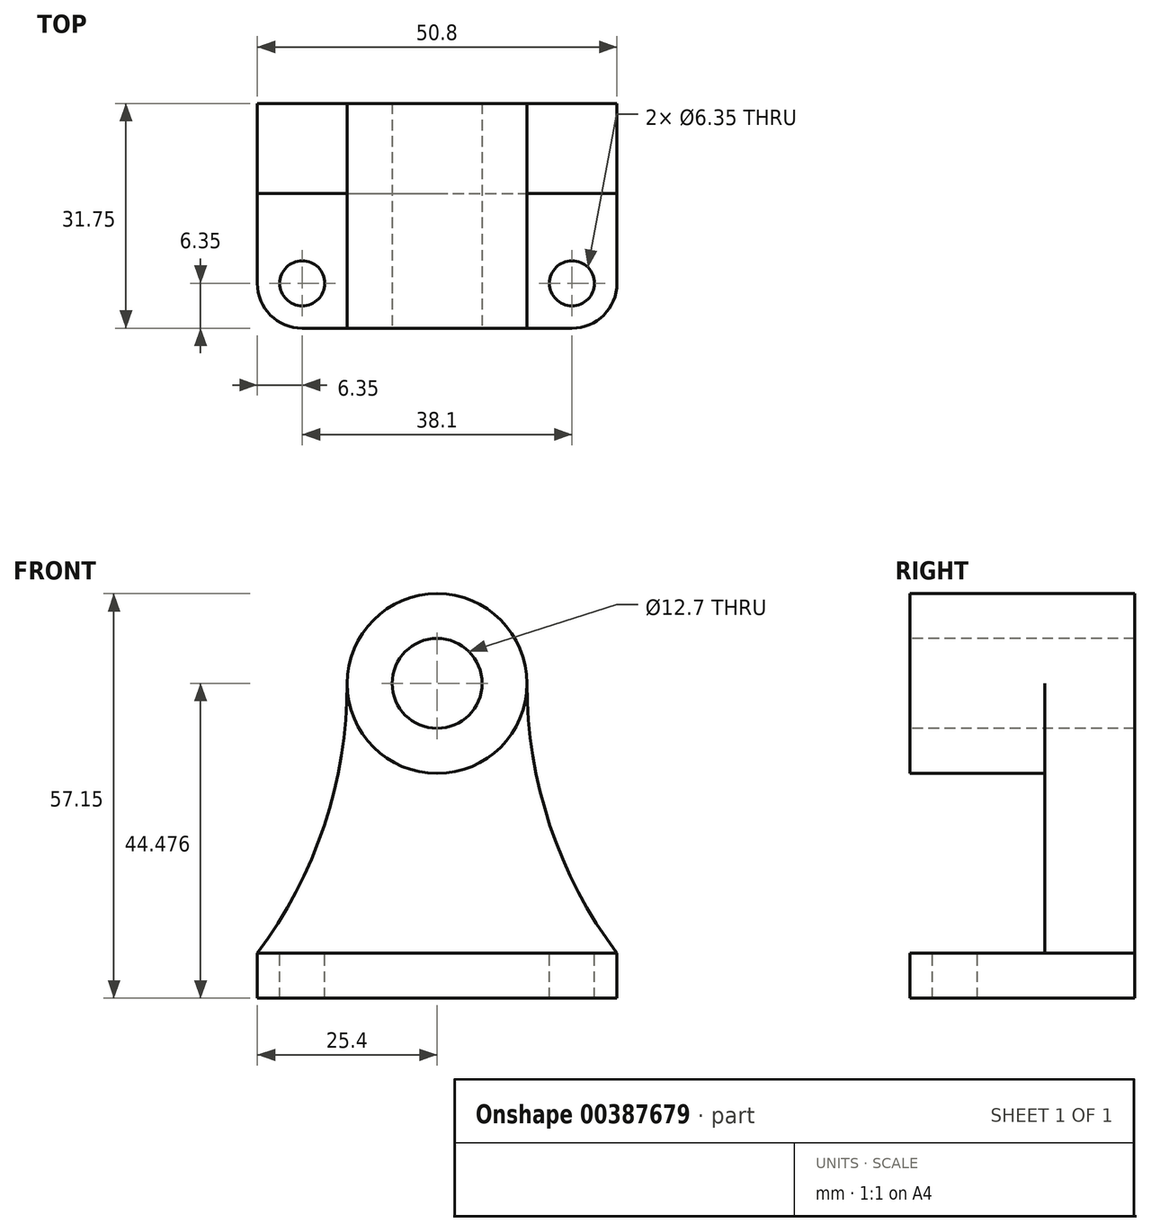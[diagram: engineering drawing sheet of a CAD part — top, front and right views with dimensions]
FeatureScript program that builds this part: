
annotation { "Feature Type Name" : "Feature", "Feature Type Description" : "" }
export const myFeature = defineFeature(function(context is Context, id is Id, definition is map)
    precondition{}
    {
        {
            var Q0;
            Q0=qCreatedBy(makeId("Front.planeOp"),FACE);
            var sketch = newSketch(context, id + "F0", { "sketchPlane" : qUnion([Q0])});
            skLineSegment(sketch, "E0", {"start": v(0, 0) * mm, "end": v(50.8, 0) * mm});
            skLineSegment(sketch, "E1", {"start": v(50.8, 0) * mm, "end": v(50.8, 6.35) * mm});
            skLineSegment(sketch, "E2", {"start": v(50.8, 6.35) * mm, "end": v(38.1, 6.35) * mm});
            skLineSegment(sketch, "E3", {"start": v(38.1, 6.35) * mm, "end": v(38.1, 57.15) * mm});
            skLineSegment(sketch, "E4", {"start": v(38.1, 57.15) * mm, "end": v(12.7, 57.15) * mm});
            skLineSegment(sketch, "E5", {"start": v(12.7, 57.15) * mm, "end": v(12.7, 6.35) * mm});
            skLineSegment(sketch, "E6", {"start": v(12.7, 6.35) * mm, "end": v(0, 6.35) * mm});
            skLineSegment(sketch, "E7", {"start": v(0, 6.35) * mm, "end": v(0, 0) * mm});
            skSolve(sketch);
        }
        {
            var Q0;
            Q0=makeQuery(id+"F0.imprint","IMPRINT",FACE,{"disambiguationData":[TD([[makeQuery(id+"F0.imprint","IMPRINT",EDGE,{"derivedFrom":sQuery(id+"F0.wireOp",EDGE,"E0")}),1.0]])]});
            extrude(context, id + "F1", {"entities" : qUnion([Q0]), "depth" : 31.75 * mm});
        }
        {
            var Q0;
            Q0=makeQuery(id+"F1.opExtrude","CAP_FACE",FACE,{"disambiguationData":[OSD([sQuery(id+"F0.wireOp",EDGE,"E0"),sQuery(id+"F0.wireOp",EDGE,"E1"),sQuery(id+"F0.wireOp",EDGE,"E2"),sQuery(id+"F0.wireOp",EDGE,"E3"),sQuery(id+"F0.wireOp",EDGE,"E4"),sQuery(id+"F0.wireOp",EDGE,"E5"),sQuery(id+"F0.wireOp",EDGE,"E6"),sQuery(id+"F0.wireOp",EDGE,"E7")])],"isStart":false});
            var sketch = newSketch(context, id + "F2", { "sketchPlane" : qUnion([Q0])});
            skCircle(sketch, "E8", {"center": v(25.4, 44.45) * mm, "radius": 12.7 * mm});
            skSolve(sketch);
        }
        {
            var Q0;
            {var subQ0=sQuery(id+"F2.wireOp",EDGE,"E8");var subQ1=makeQuery(id+"F1.opExtrude","CAP_EDGE",EDGE,{"disambiguationData":[OSD([sQuery(id+"F0.wireOp",EDGE,"E4")])],"isStart":false});var subQ2=makeQuery(id+"F2.imprint","INTERSECT",VERTEX,{"derivedFrom":[subQ1,subQ0]});Q0=makeQuery(id+"F2.imprint","IMPRINT",FACE,{"disambiguationData":[TD([[makeQuery(id+"F2.imprint","IMPRINT",EDGE,{"disambiguationData":[TD([[subQ2,-1.0]])],"derivedFrom":subQ0}),-1.0]])]});}
            var Q1;
            {var subQ0=sQuery(id+"F2.wireOp",EDGE,"E8");var subQ1=makeQuery(id+"F1.opExtrude","CAP_EDGE",EDGE,{"disambiguationData":[OSD([sQuery(id+"F0.wireOp",EDGE,"E4")])],"isStart":false});var subQ2=makeQuery(id+"F2.imprint","INTERSECT",VERTEX,{"derivedFrom":[subQ1,subQ0]});Q1=makeQuery(id+"F2.imprint","IMPRINT",FACE,{"disambiguationData":[TD([[makeQuery(id+"F2.imprint","IMPRINT",EDGE,{"disambiguationData":[TD([[subQ2,1.0]])],"derivedFrom":subQ0}),-1.0]])]});}
            extrude(context, id + "F3", {"entities" : qUnion([Q0, Q1]), "operationType" : NewBodyOperationType.REMOVE, "oppositeDirection" : true, "depth" : 31.75 * mm});
        }
        {
            var Q0;
            Q0=makeQuery(id+"F1.opExtrude","CAP_FACE",FACE,{"disambiguationData":[OSD([sQuery(id+"F0.wireOp",EDGE,"E0"),sQuery(id+"F0.wireOp",EDGE,"E1"),sQuery(id+"F0.wireOp",EDGE,"E2"),sQuery(id+"F0.wireOp",EDGE,"E3"),sQuery(id+"F0.wireOp",EDGE,"E4"),sQuery(id+"F0.wireOp",EDGE,"E5"),sQuery(id+"F0.wireOp",EDGE,"E6"),sQuery(id+"F0.wireOp",EDGE,"E7")])],"isStart":false});
            var sketch = newSketch(context, id + "F4", { "sketchPlane" : qUnion([Q0])});
            skCircle(sketch, "E9", {"center": v(25.4, 44.45) * mm, "radius": 12.7 * mm});
            skSolve(sketch);
        }
        {
            var Q0;
            Q0=makeQuery(id+"F4.imprint","IMPRINT",FACE,{"disambiguationData":[TD([[makeQuery(id+"F4.imprint","IMPRINT",EDGE,{"derivedFrom":makeQuery(id+"F1.opExtrude","CAP_EDGE",EDGE,{"disambiguationData":[OSD([sQuery(id+"F0.wireOp",EDGE,"E0")])],"isStart":false})}),1.0]])]});
            var sketch = newSketch(context, id + "F5", { "sketchPlane" : qUnion([Q0])});
            skLineSegment(sketch, "E10", {"start": v(12.7, 31.75) * mm, "end": v(38.1, 31.75) * mm});
            skSolve(sketch);
        }
        {
            var Q0;
            {var subQ0=sQuery(id+"F4.wireOp",EDGE,"E9");var subQ1=makeQuery(id+"F4.imprint","INTERSECT",VERTEX,{"derivedFrom":[makeQuery(id+"F1.opExtrude","CAP_EDGE",EDGE,{"disambiguationData":[OSD([sQuery(id+"F0.wireOp",EDGE,"E3")])],"isStart":false}),subQ0]});Q0=makeQuery(id+"F4.imprint","IMPRINT",FACE,{"disambiguationData":[TD([[makeQuery(id+"F4.imprint","IMPRINT",EDGE,{"disambiguationData":[TD([[subQ1,-1.0]])],"derivedFrom":subQ0}),1.0]])]});}
            var sketch = newSketch(context, id + "F6", { "sketchPlane" : qUnion([Q0])});
            skCircle(sketch, "E11", {"center": v(25.4, 44.48) * mm, "radius": 12.7 * mm});
            skSolve(sketch);
        }
        {
            var Q0;
            {var subQ0=sQuery(id+"F5.wireOp",EDGE,"E10");var subQ1=makeQuery(id+"F1.opExtrude","CAP_EDGE",EDGE,{"disambiguationData":[OSD([sQuery(id+"F0.wireOp",EDGE,"E3")])],"isStart":false});var subQ2=makeQuery(id+"F4.imprint","IMPRINT",EDGE,{"derivedFrom":subQ1});var subQ3=makeQuery(id+"F5.imprint","INTERSECT",VERTEX,{"derivedFrom":[subQ2,subQ0]});Q0=makeQuery(id+"F5.imprint","IMPRINT",FACE,{"disambiguationData":[TD([[makeQuery(id+"F5.imprint","IMPRINT",EDGE,{"disambiguationData":[TD([[subQ3,1.0]])],"derivedFrom":subQ0}),1.0]])]});}
            extrude(context, id + "F7", {"entities" : qUnion([Q0]), "operationType" : NewBodyOperationType.REMOVE, "oppositeDirection" : true, "depth" : 19.05 * mm});
        }
        {
            var Q0;
            Q0=makeQuery(id+"F4.imprint","IMPRINT",FACE,{"disambiguationData":[TD([[makeQuery(id+"F4.imprint","IMPRINT",EDGE,{"derivedFrom":makeQuery(id+"F1.opExtrude","CAP_EDGE",EDGE,{"disambiguationData":[OSD([sQuery(id+"F0.wireOp",EDGE,"E0")])],"isStart":false})}),1.0]])]});
            var sketch = newSketch(context, id + "F8", { "sketchPlane" : qUnion([Q0])});
            skLineSegment(sketch, "E12", {"start": v(25.64, 31.75) * mm, "end": v(12.7, 31.75) * mm});
            skSolve(sketch);
        }
        {
            var Q0;
            Q0=makeQuery(id+"F1.opExtrude","SWEPT_FACE",FACE,{"disambiguationData":[OSD([sQuery(id+"F0.wireOp",EDGE,"E0")])]});
            var sketch = newSketch(context, id + "F9", { "sketchPlane" : qUnion([Q0])});
            skLineSegment(sketch, "E13", {"start": v(0, 12.7) * mm, "end": v(50.8, 12.7) * mm});
            skSolve(sketch);
        }
        {
            var Q0;
            {var subQ0=sQuery(id+"F9.wireOp",EDGE,"E13");Q0=makeQuery(id+"F9.imprint","IMPRINT",FACE,{"disambiguationData":[TD([[makeQuery(id+"F9.imprint","IMPRINT",EDGE,{"derivedFrom":subQ0}),1.0]])]});}
            extrude(context, id + "F10", {"entities" : qUnion([Q0]), "operationType" : NewBodyOperationType.REMOVE, "oppositeDirection" : true, "depth" : 31.75 * mm});
        }
        {
            var Q0;
            {var subQ0=sQuery(id+"F8.wireOp",EDGE,"E12");var subQ1=makeQuery(id+"F1.opExtrude","CAP_EDGE",EDGE,{"disambiguationData":[OSD([sQuery(id+"F0.wireOp",EDGE,"E5")])],"isStart":false});var subQ2=makeQuery(id+"F4.imprint","IMPRINT",EDGE,{"derivedFrom":subQ1});var subQ3=makeQuery(id+"F8.imprint","INTERSECT",VERTEX,{"derivedFrom":[subQ2,subQ0]});Q0=makeQuery(id+"F8.imprint","IMPRINT",FACE,{"disambiguationData":[TD([[makeQuery(id+"F8.imprint","IMPRINT",EDGE,{"disambiguationData":[TD([[subQ3,1.0]])],"derivedFrom":subQ0}),-1.0]])]});}
            extrude(context, id + "F11", {"entities" : qUnion([Q0]), "operationType" : NewBodyOperationType.REMOVE, "oppositeDirection" : true, "depth" : 19.05 * mm});
        }
        {
            var Q0;
            {var subQ0=sQuery(id+"F4.wireOp",EDGE,"E9");Q0=makeQuery(id+"F11.boolean.opBoolean","MERGE",FACE,{"derivedFrom":[makeQuery(id+"F10.boolean.opBoolean","MERGE",FACE,{"derivedFrom":[makeQuery(id+"F7.boolean.opBoolean","COPY",FACE,{"derivedFrom":makeQuery(id+"F7.opExtrude","CAP_FACE",FACE,{"disambiguationData":[OSD([sQuery(id+"F0.wireOp",EDGE,"E3"),subQ0,sQuery(id+"F5.wireOp",EDGE,"E10")])],"isStart":false})}),makeQuery(id+"F10.opExtrude","SWEPT_FACE",FACE,{"disambiguationData":[OSD([sQuery(id+"F9.wireOp",EDGE,"E13")])]})]}),makeQuery(id+"F11.opExtrude","CAP_FACE",FACE,{"disambiguationData":[OSD([sQuery(id+"F0.wireOp",EDGE,"E5"),subQ0,sQuery(id+"F8.wireOp",EDGE,"E12")])],"isStart":false})]});}
            var sketch = newSketch(context, id + "F12", { "sketchPlane" : qUnion([Q0])});
            skLineSegment(sketch, "E14", {"start": v(12.7, 6.35) * mm, "end": v(38.1, 6.35) * mm});
            skSolve(sketch);
        }
        {
            var Q0;
            Q0=makeQuery(id+"F12.imprint","IMPRINT",FACE,{"disambiguationData":[TD([[makeQuery(id+"F12.imprint","IMPRINT",EDGE,{"derivedFrom":sQuery(id+"F12.wireOp",EDGE,"E14")}),-1.0]])]});
            extrude(context, id + "F13", {"entities" : qUnion([Q0]), "operationType" : NewBodyOperationType.ADD, "depth" : 19.05 * mm});
        }
        {
            var Q0;
            Q0=makeQuery(id+"F1.opExtrude","SWEPT_FACE",FACE,{"disambiguationData":[OSD([sQuery(id+"F0.wireOp",EDGE,"E5")])]});
            extrude(context, id + "F14", {"entities" : qUnion([Q0]), "operationType" : NewBodyOperationType.ADD, "depth" : 12.7 * mm});
        }
        {
            var Q0;
            Q0=makeQuery(id+"F1.opExtrude","SWEPT_FACE",FACE,{"disambiguationData":[OSD([sQuery(id+"F0.wireOp",EDGE,"E3")])]});
            extrude(context, id + "F15", {"entities" : qUnion([Q0]), "operationType" : NewBodyOperationType.ADD, "depth" : 12.7 * mm});
        }
        {
            var Q0;
            {var subQ0=sQuery(id+"F9.wireOp",EDGE,"E13");var subQ1=sQuery(id+"F0.wireOp",EDGE,"E3");var subQ2=sQuery(id+"F0.wireOp",EDGE,"E5");var subQ3=sQuery(id+"F4.wireOp",EDGE,"E9");Q0=makeQuery(id+"F15.boolean.opBoolean","MERGE",FACE,{"derivedFrom":[makeQuery(id+"F14.boolean.opBoolean","MERGE",FACE,{"derivedFrom":[makeQuery(id+"F11.boolean.opBoolean","MERGE",FACE,{"derivedFrom":[makeQuery(id+"F10.boolean.opBoolean","MERGE",FACE,{"derivedFrom":[makeQuery(id+"F7.boolean.opBoolean","COPY",FACE,{"derivedFrom":makeQuery(id+"F7.opExtrude","CAP_FACE",FACE,{"disambiguationData":[OSD([subQ1,subQ3,sQuery(id+"F5.wireOp",EDGE,"E10")])],"isStart":false})}),makeQuery(id+"F10.opExtrude","SWEPT_FACE",FACE,{"disambiguationData":[OSD([subQ0])]})]}),makeQuery(id+"F11.opExtrude","CAP_FACE",FACE,{"disambiguationData":[OSD([subQ2,subQ3,sQuery(id+"F8.wireOp",EDGE,"E12")])],"isStart":false})]}),makeQuery(id+"F14.opExtrude","SWEPT_FACE",FACE,{"disambiguationData":[OSD([subQ2,subQ0])]})]}),makeQuery(id+"F15.opExtrude","SWEPT_FACE",FACE,{"disambiguationData":[OSD([subQ1,subQ0])]})]});}
            var sketch = newSketch(context, id + "F16", { "sketchPlane" : qUnion([Q0])});
            skArc(sketch, "E15", {"start": v(0, 6.35) * mm, "mid": v(9.44, 24.37) * mm, "end": v(12.7, 44.45) * mm});
            skArc(sketch, "E16", {"start": v(38.1, 44.45) * mm, "mid": v(41.36, 24.37) * mm, "end": v(50.8, 6.35) * mm});
            skSolve(sketch);
        }
        {
            var Q0;
            Q0=makeQuery(id+"F16.imprint","IMPRINT",FACE,{"disambiguationData":[TD([[makeQuery(id+"F16.imprint","IMPRINT",EDGE,{"derivedFrom":sQuery(id+"F16.wireOp",EDGE,"E15")}),1.0]])]});
            var Q1;
            Q1=makeQuery(id+"F16.imprint","IMPRINT",FACE,{"disambiguationData":[TD([[makeQuery(id+"F16.imprint","IMPRINT",EDGE,{"derivedFrom":sQuery(id+"F16.wireOp",EDGE,"E16")}),1.0]])]});
            extrude(context, id + "F17", {"entities" : qUnion([Q0, Q1]), "operationType" : NewBodyOperationType.REMOVE, "oppositeDirection" : true, "depth" : 12.7 * mm});
        }
        {
            var Q0;
            {var subQ0=sQuery(id+"F6.wireOp",EDGE,"E11");var subQ1=sQuery(id+"F4.wireOp",EDGE,"E9");var subQ2=makeQuery(id+"F4.imprint","INTERSECT",VERTEX,{"derivedFrom":[makeQuery(id+"F1.opExtrude","CAP_EDGE",EDGE,{"disambiguationData":[OSD([sQuery(id+"F0.wireOp",EDGE,"E3")])],"isStart":false}),subQ1]});var subQ4=makeQuery(id+"F4.imprint","IMPRINT",EDGE,{"disambiguationData":[TD([[subQ2,-1.0]])],"derivedFrom":subQ1});var subQ5=makeQuery(id+"F6.imprint","INTERSECT",VERTEX,{"disambiguationData":[OD(0.0)],"derivedFrom":[subQ4,subQ0]});Q0=makeQuery(id+"F6.imprint","IMPRINT",FACE,{"disambiguationData":[TD([[makeQuery(id+"F6.imprint","IMPRINT",EDGE,{"disambiguationData":[TD([[subQ5,1.0]])],"derivedFrom":subQ0}),1.0]])]});}
            var sketch = newSketch(context, id + "F18", { "sketchPlane" : qUnion([Q0])});
            skCircle(sketch, "E17", {"center": v(25.4, 44.48) * mm, "radius": 6.35 * mm});
            skSolve(sketch);
        }
        {
            var Q0;
            Q0=makeQuery(id+"F18.imprint","IMPRINT",FACE,{"disambiguationData":[TD([[makeQuery(id+"F18.imprint","IMPRINT",EDGE,{"derivedFrom":sQuery(id+"F18.wireOp",EDGE,"E17")}),1.0]])]});
            extrude(context, id + "F19", {"entities" : qUnion([Q0]), "operationType" : NewBodyOperationType.REMOVE, "oppositeDirection" : true, "depth" : 31.75 * mm});
        }
        {
            var Q0;
            {var subQ0=sQuery(id+"F0.wireOp",EDGE,"E6");var subQ1=sQuery(id+"F0.wireOp",EDGE,"E2");Q0=makeQuery(id+"F13.boolean.opBoolean","MERGE",FACE,{"derivedFrom":[makeQuery(id+"F1.opExtrude","SWEPT_FACE",FACE,{"disambiguationData":[OSD([subQ1])]}),makeQuery(id+"F1.opExtrude","SWEPT_FACE",FACE,{"disambiguationData":[OSD([subQ0])]}),makeQuery(id+"F13.opExtrude","SWEPT_FACE",FACE,{"disambiguationData":[OSD([subQ1,subQ0,sQuery(id+"F9.wireOp",EDGE,"E13"),sQuery(id+"F12.wireOp",EDGE,"E14")])]})]});}
            var sketch = newSketch(context, id + "F20", { "sketchPlane" : qUnion([Q0])});
            skCircle(sketch, "E18", {"center": v(6.35, -25.4) * mm, "radius": 3.18 * mm});
            skCircle(sketch, "E19", {"center": v(44.45, -25.4) * mm, "radius": 3.18 * mm});
            skSolve(sketch);
        }
        {
            var Q0;
            Q0=makeQuery(id+"F20.imprint","IMPRINT",FACE,{"disambiguationData":[TD([[makeQuery(id+"F20.imprint","IMPRINT",EDGE,{"derivedFrom":sQuery(id+"F20.wireOp",EDGE,"E19")}),1.0]])]});
            var Q1;
            Q1=makeQuery(id+"F20.imprint","IMPRINT",FACE,{"disambiguationData":[TD([[makeQuery(id+"F20.imprint","IMPRINT",EDGE,{"derivedFrom":sQuery(id+"F20.wireOp",EDGE,"E18")}),1.0]])]});
            extrude(context, id + "F21", {"entities" : qUnion([Q0, Q1]), "operationType" : NewBodyOperationType.REMOVE, "oppositeDirection" : true, "depth" : 6.35 * mm});
        }
        {
            var Q0;
            {var subQ0=sQuery(id+"F0.wireOp",EDGE,"E6");var subQ1=sQuery(id+"F0.wireOp",EDGE,"E2");Q0=makeQuery(id+"F13.boolean.opBoolean","MERGE",FACE,{"derivedFrom":[makeQuery(id+"F1.opExtrude","SWEPT_FACE",FACE,{"disambiguationData":[OSD([subQ1])]}),makeQuery(id+"F1.opExtrude","SWEPT_FACE",FACE,{"disambiguationData":[OSD([subQ0])]}),makeQuery(id+"F13.opExtrude","SWEPT_FACE",FACE,{"disambiguationData":[OSD([subQ1,subQ0,sQuery(id+"F9.wireOp",EDGE,"E13"),sQuery(id+"F12.wireOp",EDGE,"E14")])]})]});}
            var sketch = newSketch(context, id + "F22", { "sketchPlane" : qUnion([Q0])});
            skArc(sketch, "E20", {"start": v(0, -25.4) * mm, "mid": v(1.86, -29.9) * mm, "end": v(6.35, -31.75) * mm});
            skSolve(sketch);
        }
        {
            var Q0;
            {var subQ0=sQuery(id+"F22.wireOp",EDGE,"E20");Q0=makeQuery(id+"F22.imprint","IMPRINT",FACE,{"disambiguationData":[TD([[makeQuery(id+"F22.imprint","IMPRINT",EDGE,{"derivedFrom":subQ0}),-1.0]])]});}
            extrude(context, id + "F23", {"entities" : qUnion([Q0]), "operationType" : NewBodyOperationType.REMOVE, "oppositeDirection" : true, "depth" : 6.35 * mm});
        }
        {
            var Q0;
            {var subQ0=sQuery(id+"F0.wireOp",EDGE,"E6");var subQ1=sQuery(id+"F0.wireOp",EDGE,"E2");Q0=makeQuery(id+"F13.boolean.opBoolean","MERGE",FACE,{"derivedFrom":[makeQuery(id+"F1.opExtrude","SWEPT_FACE",FACE,{"disambiguationData":[OSD([subQ1])]}),makeQuery(id+"F1.opExtrude","SWEPT_FACE",FACE,{"disambiguationData":[OSD([subQ0])]}),makeQuery(id+"F13.opExtrude","SWEPT_FACE",FACE,{"disambiguationData":[OSD([subQ1,subQ0,sQuery(id+"F9.wireOp",EDGE,"E13"),sQuery(id+"F12.wireOp",EDGE,"E14")])]})]});}
            var sketch = newSketch(context, id + "F24", { "sketchPlane" : qUnion([Q0])});
            skArc(sketch, "E21", {"start": v(44.45, -31.75) * mm, "mid": v(48.94, -29.9) * mm, "end": v(50.8, -25.4) * mm});
            skSolve(sketch);
        }
        {
            var Q0;
            {var subQ0=sQuery(id+"F24.wireOp",EDGE,"E21");Q0=makeQuery(id+"F24.imprint","IMPRINT",FACE,{"disambiguationData":[TD([[makeQuery(id+"F24.imprint","IMPRINT",EDGE,{"derivedFrom":subQ0}),-1.0]])]});}
            extrude(context, id + "F25", {"entities" : qUnion([Q0]), "operationType" : NewBodyOperationType.REMOVE, "oppositeDirection" : true, "depth" : 6.35 * mm});
        }
    });
